# Revit family: Ceileo-SQ
name_source: partatom
category: Lighting Fixtures
revit_build: Autodesk Revit Architecture 2012 (Build: 20110309_2315(x64)
units: mm (PartAtom-declared; Revit-internal decimal feet)

## types (12) — shared parameters
Apparent Load = 55 VA
Default Elevation = 48"
Description = Ceileo is a commercial grade LED canopy luminaire that utilizes high powered LED’s with precise efficient optical control and on board wattage and lumen choices.
Glass = Hubbell- White Glass
Lamp = LED Lamp
Manufacturer = Beacon Lighting
Manufacturer Fax = (941) 751-5535
Model = CLO SQ
Nominal Watts = 55 W
Product Documentation Link = http://www.beaconproducts.com
Product Page URL = http://www.beaconproducts.com
URL = http://www.beaconproducts.com
Voltage = 120 V

## per-type parameters (varying)
| type | Backbox | Photometric Web |
| CLO SQ-BBT | Hubbell- Paint- Black Textured | Web CLO : CLO-24NB-55-3K-5X5 |
| CLO SQ-BMT | Hubbell- Paint- Black Matte Textured | Web CLO : CLO-24NB-55-3K-5X5 |
| CLO SQ-WHT | Hubbell- Paint- White | Web CLO : CLO-24NB-55-3K-5X5 |
| CLO SQ-BZT | Hubbell- Paint- Bronze Textured | Web CLO : CLO-24NB-55-5K-T5SQN |
| CLO SQ-MBT | Hubbell- Paint- Mettalic Bronze Textured | Web CLO : CLO-24NB-55-3K-5X5 |
| CLO SQ-DBT | Hubbell- Paint- Dark  Bronze Textured | Web CLO : CLO-24NB-55-3K-5X5 |
| CLO SQ-GYS | Hubbell- Paint- Grey smooth | Web CLO : CLO-24NB-55-3K-5X5 |
| CLO SQ-DPS | Hubbell- Paint- Dark Platinum Smooth | Web CLO : CLO-24NB-55-3K-5X5 |
| CLO SQ-GNT | Hubbell- Paint- Green Textured | Web CLO : CLO-24NB-55-3K-5X5 |
| CLO SQ-MST | Hubbell- Paint- Mettallic Silver Textured | Web CLO : CLO-24NB-55-3K-5X5 |
| CLO SQ-MTT | Hubbell- Paint- Metallic titanium textured | Web CLO : CLO-24NB-55-3K-5X5 |
| CLO SQ-OWI | Hubbell- Paint- Old World Iron | Web CLO : CLO-24NB-55-3K-5X5 |

## geometry (parser evidence)
native form markers: Blend x16, Sweep x4
no freeform markers — native parametric forms only
